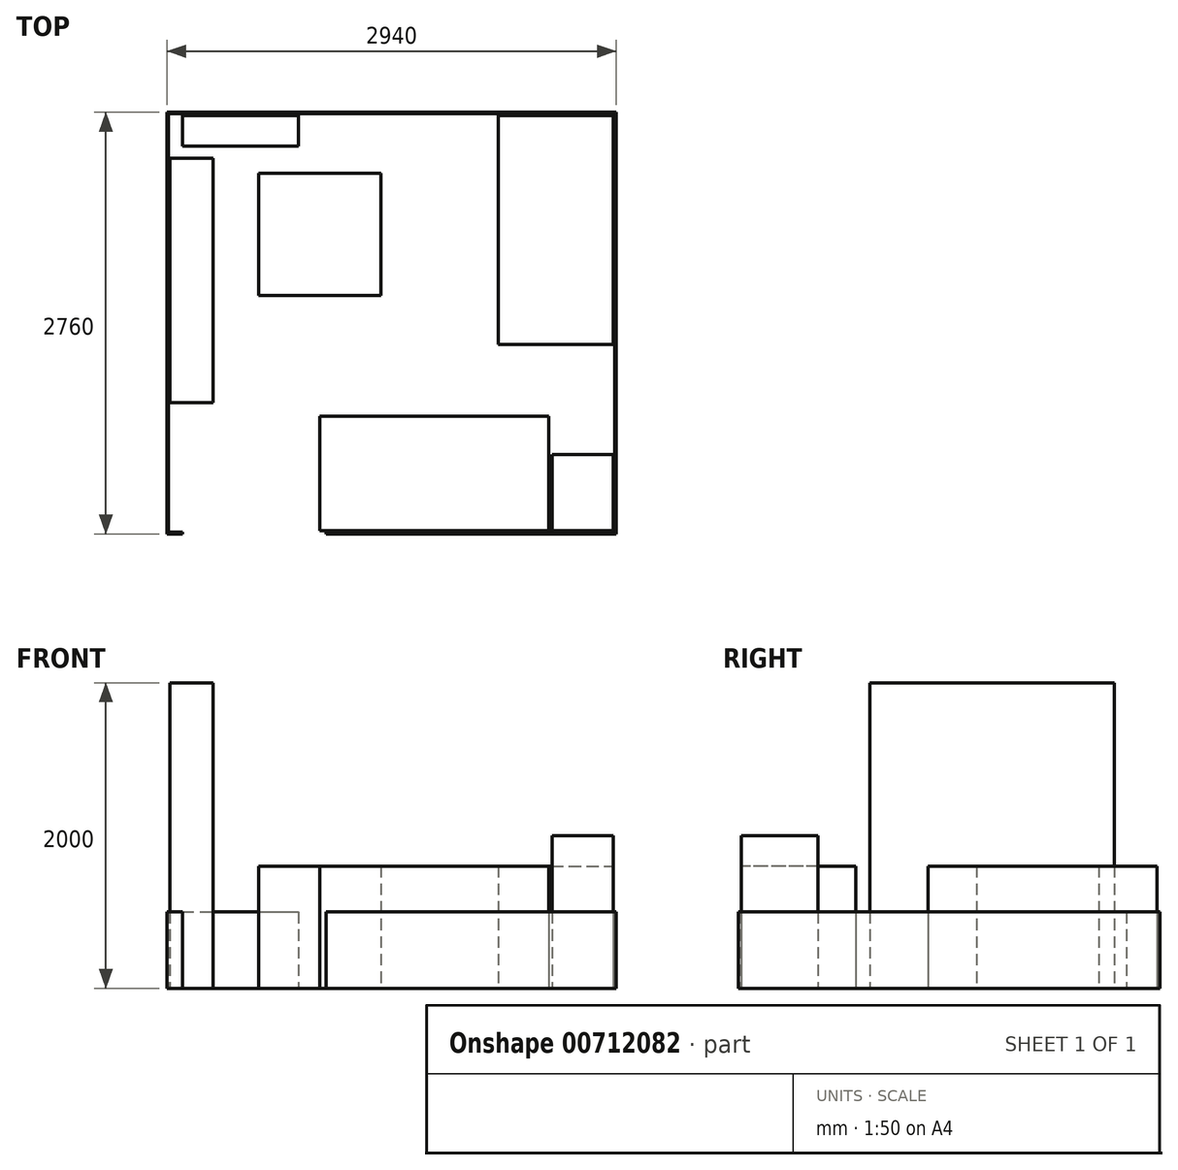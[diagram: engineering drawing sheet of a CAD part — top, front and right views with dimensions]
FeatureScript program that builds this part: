
annotation { "Feature Type Name" : "Feature", "Feature Type Description" : "" }
export const myFeature = defineFeature(function(context is Context, id is Id, definition is map)
    precondition{}
    {
        {
            var Q0;
            Q0=qCreatedBy(makeId("Top.planeOp"),FACE);
            var sketch = newSketch(context, id + "F0", { "sketchPlane" : qUnion([Q0])});
            skLineSegment(sketch, "E0.bottom", {"start": v(-1490, 1990) * mm, "end": v(1430, 1990) * mm});
            skLineSegment(sketch, "E0.top", {"start": v(-1490, -750) * mm, "end": v(-1400, -750) * mm});
            skLineSegment(sketch, "E0.left", {"start": v(-1490, 1990) * mm, "end": v(-1490, -750) * mm});
            skLineSegment(sketch, "E0.right", {"start": v(1430, 1990) * mm, "end": v(1430, -750) * mm});
            skLineSegment(sketch, "E1.0", {"start": v(-1500, 2000) * mm, "end": v(-1500, -760) * mm});
            skLineSegment(sketch, "E1.1", {"start": v(-1500, 2000) * mm, "end": v(1440, 2000) * mm});
            skLineSegment(sketch, "E1.2", {"start": v(1440, 2000) * mm, "end": v(1440, -760) * mm});
            skLineSegment(sketch, "E1.3", {"start": v(-1500, -760) * mm, "end": v(-1400, -760) * mm});
            skLineSegment(sketch, "E2", {"start": v(-1400, -750) * mm, "end": v(-1400, -760) * mm});
            skLineSegment(sketch, "E3", {"start": v(-460, -750) * mm, "end": v(-460, -760) * mm});
            skLineSegment(sketch, "E4.trimOffspring", {"start": v(-460, -750) * mm, "end": v(1430, -750) * mm});
            skLineSegment(sketch, "E5.trimOffspring", {"start": v(-460, -760) * mm, "end": v(1440, -760) * mm});
            skLineSegment(sketch, "E6.bottom", {"start": v(-500, 10) * mm, "end": v(1000, 10) * mm});
            skLineSegment(sketch, "E6.top", {"start": v(-500, -740) * mm, "end": v(1000, -740) * mm});
            skLineSegment(sketch, "E6.left", {"start": v(-500, 10) * mm, "end": v(-500, -740) * mm});
            skLineSegment(sketch, "E6.right", {"start": v(1000, 10) * mm, "end": v(1000, -740) * mm});
            skLineSegment(sketch, "E7.bottom", {"start": v(-1480, 100) * mm, "end": v(-1200, 100) * mm});
            skLineSegment(sketch, "E7.top", {"start": v(-1480, 1700) * mm, "end": v(-1200, 1700) * mm});
            skLineSegment(sketch, "E7.left", {"start": v(-1480, 100) * mm, "end": v(-1480, 1700) * mm});
            skLineSegment(sketch, "E7.right", {"start": v(-1200, 100) * mm, "end": v(-1200, 1700) * mm});
            skLineSegment(sketch, "E8.bottom", {"start": v(670, 1980) * mm, "end": v(1420, 1980) * mm});
            skLineSegment(sketch, "E8.top", {"start": v(670, 480) * mm, "end": v(1420, 480) * mm});
            skLineSegment(sketch, "E8.left", {"start": v(670, 1980) * mm, "end": v(670, 480) * mm});
            skLineSegment(sketch, "E8.right", {"start": v(1420, 1980) * mm, "end": v(1420, 480) * mm});
            skLineSegment(sketch, "E9.bottom", {"start": v(1020, -740) * mm, "end": v(1420, -740) * mm});
            skLineSegment(sketch, "E9.top", {"start": v(1020, -240) * mm, "end": v(1420, -240) * mm});
            skLineSegment(sketch, "E9.left", {"start": v(1020, -740) * mm, "end": v(1020, -240) * mm});
            skLineSegment(sketch, "E9.right", {"start": v(1420, -740) * mm, "end": v(1420, -240) * mm});
            skLineSegment(sketch, "E10.bottom", {"start": v(-1400, 1980) * mm, "end": v(-640, 1980) * mm});
            skLineSegment(sketch, "E10.top", {"start": v(-1400, 1780) * mm, "end": v(-640, 1780) * mm});
            skLineSegment(sketch, "E10.left", {"start": v(-1400, 1980) * mm, "end": v(-1400, 1780) * mm});
            skLineSegment(sketch, "E10.right", {"start": v(-640, 1980) * mm, "end": v(-640, 1780) * mm});
            skLineSegment(sketch, "E11.bottom", {"start": v(-900, 1600) * mm, "end": v(-100, 1600) * mm});
            skLineSegment(sketch, "E11.top", {"start": v(-900, 800) * mm, "end": v(-100, 800) * mm});
            skLineSegment(sketch, "E11.left", {"start": v(-900, 1600) * mm, "end": v(-900, 800) * mm});
            skLineSegment(sketch, "E11.right", {"start": v(-100, 1600) * mm, "end": v(-100, 800) * mm});
            skSolve(sketch);
        }
        {
            var Q0;
            Q0=makeQuery(id+"F0.imprint","IMPRINT",FACE,{"disambiguationData":[TD([[makeQuery(id+"F0.imprint","IMPRINT",EDGE,{"derivedFrom":sQuery(id+"F0.wireOp",EDGE,"E0.bottom")}),1.0]])]});
            extrude(context, id + "F1", {"entities" : qUnion([Q0]), "depth" : 500 * mm, "offsetDistance" : 25 * mm});
        }
        {
            var Q0;
            Q0=makeQuery(id+"F0.imprint","IMPRINT",FACE,{"disambiguationData":[TD([[makeQuery(id+"F0.imprint","IMPRINT",EDGE,{"derivedFrom":sQuery(id+"F0.wireOp",EDGE,"E7.bottom")}),1.0]])]});
            extrude(context, id + "F2", {"entities" : qUnion([Q0]), "depth" : 2000 * mm, "offsetDistance" : 25 * mm});
        }
        {
            var Q0;
            Q0=makeQuery(id+"F0.imprint","IMPRINT",FACE,{"disambiguationData":[TD([[makeQuery(id+"F0.imprint","IMPRINT",EDGE,{"derivedFrom":sQuery(id+"F0.wireOp",EDGE,"E10.bottom")}),-1.0]])]});
            extrude(context, id + "F3", {"entities" : qUnion([Q0]), "depth" : 500 * mm, "offsetDistance" : 25 * mm});
        }
        {
            var Q0;
            Q0=makeQuery(id+"F0.imprint","IMPRINT",FACE,{"disambiguationData":[TD([[makeQuery(id+"F0.imprint","IMPRINT",EDGE,{"derivedFrom":sQuery(id+"F0.wireOp",EDGE,"E11.bottom")}),-1.0]])]});
            extrude(context, id + "F4", {"entities" : qUnion([Q0]), "depth" : 800 * mm, "offsetDistance" : 25 * mm});
        }
        {
            var Q0;
            Q0=makeQuery(id+"F0.imprint","IMPRINT",FACE,{"disambiguationData":[TD([[makeQuery(id+"F0.imprint","IMPRINT",EDGE,{"derivedFrom":sQuery(id+"F0.wireOp",EDGE,"E9.bottom")}),1.0]])]});
            extrude(context, id + "F5", {"entities" : qUnion([Q0]), "depth" : 1000 * mm, "offsetDistance" : 25 * mm});
        }
        {
            var Q0;
            Q0=makeQuery(id+"F0.imprint","IMPRINT",FACE,{"disambiguationData":[TD([[makeQuery(id+"F0.imprint","IMPRINT",EDGE,{"derivedFrom":sQuery(id+"F0.wireOp",EDGE,"E6.bottom")}),-1.0]])]});
            extrude(context, id + "F6", {"entities" : qUnion([Q0]), "depth" : 800 * mm, "offsetDistance" : 25 * mm});
        }
        {
            var Q0;
            Q0=makeQuery(id+"F0.imprint","IMPRINT",FACE,{"disambiguationData":[TD([[makeQuery(id+"F0.imprint","IMPRINT",EDGE,{"derivedFrom":sQuery(id+"F0.wireOp",EDGE,"E8.bottom")}),-1.0]])]});
            extrude(context, id + "F7", {"entities" : qUnion([Q0]), "depth" : 800 * mm, "offsetDistance" : 25 * mm});
        }
    });
